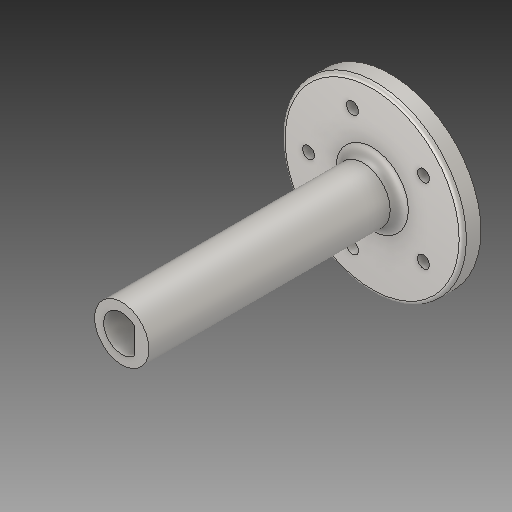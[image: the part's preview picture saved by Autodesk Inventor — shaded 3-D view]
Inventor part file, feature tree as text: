
AUTODESK INVENTOR PART (.ipt)
format: ipt  version: 2019 (Build 230136000, 136)  size: 176,128 bytes
history: native  units: mm
features: sketch x3, extrude x2, fillet x2, hole x1, pattern_circular x1, projected_geometry x1
ambient origin geometry x8: Origin, YZ Plane, XZ Plane, XY Plane, X Axis, Y Axis, Z Axis, Center Point
bodies: Solid1 (feature_tree)
feature tree (10):
  extrude  "Extrusion1"  Depth=20.0mm
  extrude  "Extrusion2"  Depth=2.0mm
  fillet  "Fillet1"  Radius=138.0mm
  fillet  "Fillet2"  Radius=2.0mm
  hole  "Hole1"  [1 undecoded]
  pattern_circular  "Circular Pattern1"  [2 undecoded]
  sketch  "Sketch2"  dims[d2=100.0mm d3=20.0mm]
  sketch  "Sketch3"  dims[d4=10.0mm d5=0.0mm d6=30.0mm d7=138.0mm d8=0.0mm d9=2.0mm]
  sketch  "Sketch4"  dims[d10=5.0mm d11=35.0mm d12=12.0mm d13=6.6mm d14=8.918mm d15=13.44mm d16=2.0mm d17=90.0deg d18=8.0mm d19=20.594885mm d20=50.0mm d21=360.0deg d23=14.0mm]
  projected_geometry  "Projected Loop1"
note: 3 required parameter values undecoded (feature->parameter linkage not recoverable at this tier; creation-order binding heuristic only, values carry confidence <= 0.55)
